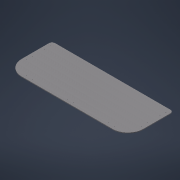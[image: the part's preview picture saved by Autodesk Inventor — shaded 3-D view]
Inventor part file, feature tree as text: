
AUTODESK INVENTOR PART (.ipt)
format: ipt  version: 2022 (Build 260153000, 153)  size: 131,072 bytes
history: native  units: mm
features: sketch x2, extrude x1, hole x1
ambient origin geometry x8: Origin, YZ Plane, XZ Plane, XY Plane, X Axis, Y Axis, Z Axis, Center Point
bodies: Solid1 (feature_tree)
feature tree (4):
  sketch  "Sketch1"  dims[d0=800.0mm d1=300.0mm]
  extrude  "Extrusion1"  Depth=300.0mm
  hole  "Hole1"  [1 undecoded]
  sketch  "Sketch2"  dims[d2=100.0mm d3=20.0mm d4=5.0mm d5=0.0mm d7=40.0mm d8=20.0mm d9=500.0mm d10=40.0mm d11=40.0mm d12=80.0mm d14=20.0mm d15=3.4mm d16=6.0mm d17=6.5mm d18=3.4mm d19=90.0deg d20=8.0mm d21=20.594885mm d23=40.0mm]
note: 1 required parameter value undecoded (feature->parameter linkage not recoverable at this tier; creation-order binding heuristic only, values carry confidence <= 0.55)
